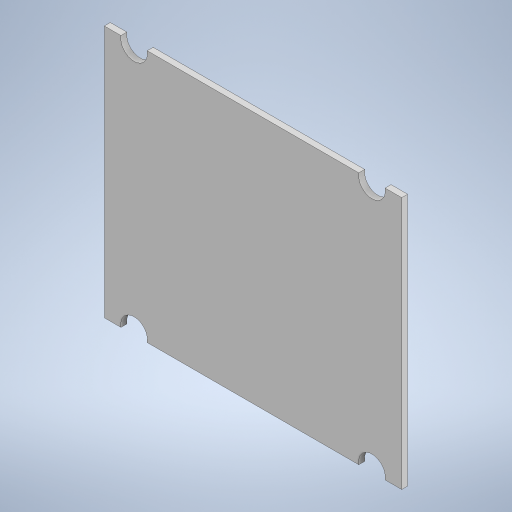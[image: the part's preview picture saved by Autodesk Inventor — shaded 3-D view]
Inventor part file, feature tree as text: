
AUTODESK INVENTOR PART (.ipt)
format: ipt  version: 2023 (Build 270158000, 158)  size: 211,456 bytes
history: native  units: mm
features: extrude x2, sketch x2, other x1
ambient origin geometry x8: Origin, YZ Plane, XZ Plane, XY Plane, X Axis, Y Axis, Z Axis, Center Point
bodies: Body1 (feature_tree)
feature tree (5):
  other  "솔리드1"
  extrude  "돌출1"  Depth=30.0mm
  extrude  "돌출2"  Depth=25.5mm
  sketch  "스케치1"
  sketch  "스케치2"
